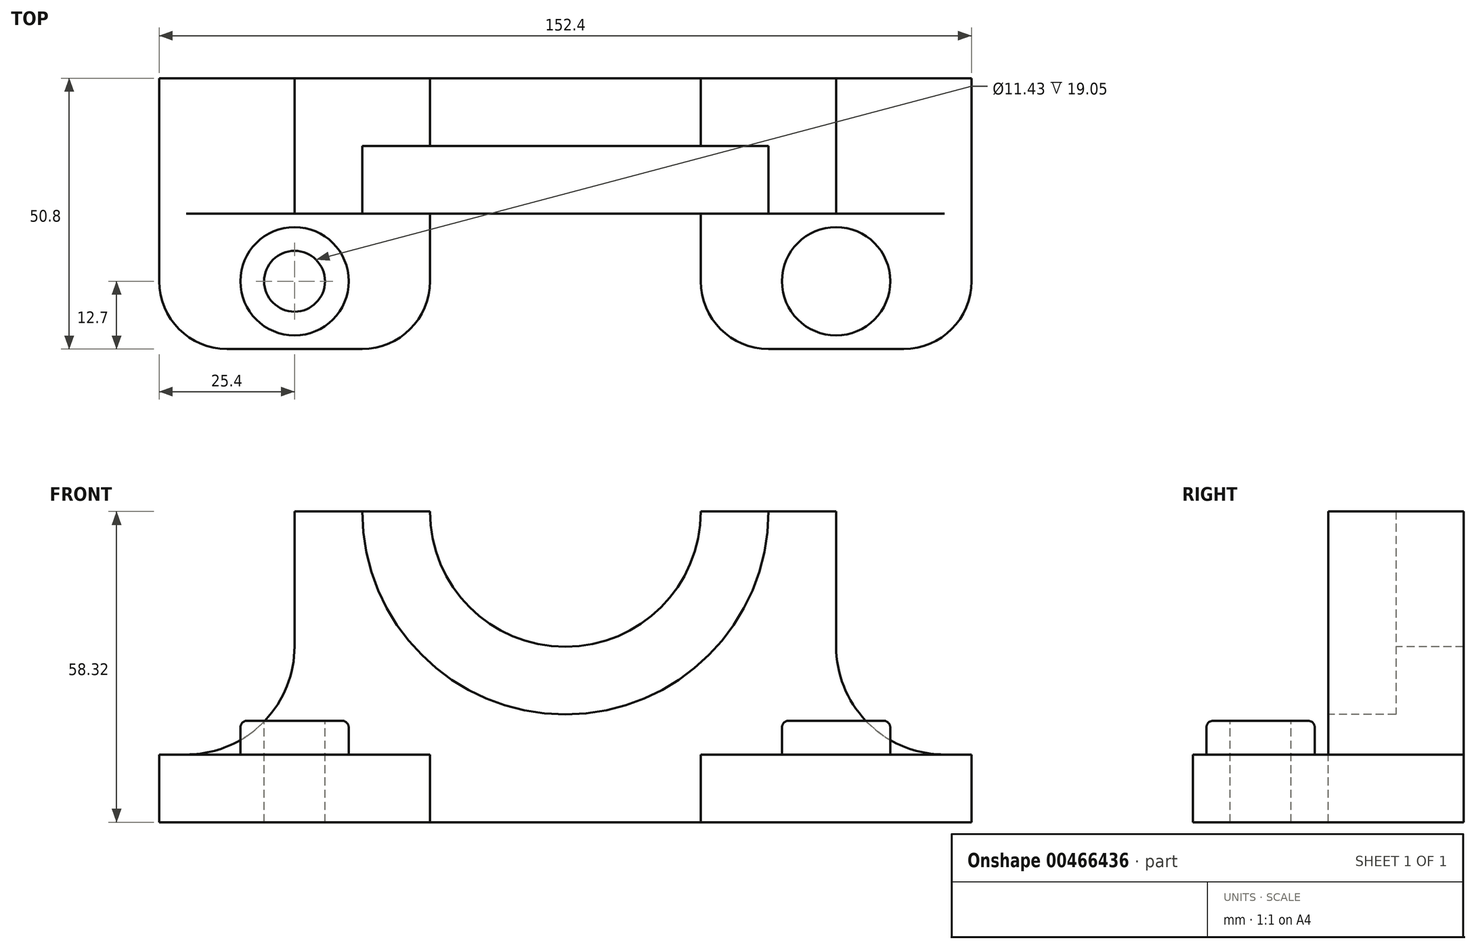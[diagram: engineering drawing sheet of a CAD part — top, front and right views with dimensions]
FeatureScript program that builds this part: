
annotation { "Feature Type Name" : "Feature", "Feature Type Description" : "" }
export const myFeature = defineFeature(function(context is Context, id is Id, definition is map)
    precondition{}
    {
        {
            var Q0;
            Q0=qCreatedBy(makeId("Front.planeOp"),FACE);
            var sketch = newSketch(context, id + "F0", { "sketchPlane" : qUnion([Q0])});
            skLineSegment(sketch, "E0.bottom", {"start": v(-50.8, 0) * mm, "end": v(50.8, 0) * mm});
            skLineSegment(sketch, "E0.top", {"start": v(-50.8, 58.32) * mm, "end": v(50.8, 58.32) * mm});
            skLineSegment(sketch, "E0.left", {"start": v(-50.8, 0) * mm, "end": v(-50.8, 58.32) * mm});
            skLineSegment(sketch, "E0.right", {"start": v(50.8, 0) * mm, "end": v(50.8, 58.32) * mm});
            skSolve(sketch);
        }
        {
            var Q0;
            Q0=qCreatedBy(makeId("Front.planeOp"),FACE);
            var sketch = newSketch(context, id + "F1", { "sketchPlane" : qUnion([Q0])});
            skLineSegment(sketch, "E1.bottom", {"start": v(-76.2, 12.7) * mm, "end": v(-25.4, 12.7) * mm});
            skLineSegment(sketch, "E1.top", {"start": v(-76.2, 0) * mm, "end": v(-25.4, 0) * mm});
            skLineSegment(sketch, "E1.left", {"start": v(-76.2, 12.7) * mm, "end": v(-76.2, 0) * mm});
            skLineSegment(sketch, "E1.right", {"start": v(-25.4, 12.7) * mm, "end": v(-25.4, 0) * mm});
            skLineSegment(sketch, "E2.MirrorCS", {"start": v(76.2, 12.7) * mm, "end": v(25.4, 12.7) * mm});
            skLineSegment(sketch, "E3.MirrorCS", {"start": v(76.2, 12.7) * mm, "end": v(76.2, 0) * mm});
            skLineSegment(sketch, "E4.MirrorCS", {"start": v(76.2, 0) * mm, "end": v(25.4, 0) * mm});
            skLineSegment(sketch, "E5.MirrorCS", {"start": v(25.4, 12.7) * mm, "end": v(25.4, 0) * mm});
            skSolve(sketch);
        }
        {
            var Q0;
            Q0=makeQuery(id+"F0.imprint","IMPRINT",FACE,{"disambiguationData":[TD([[makeQuery(id+"F0.imprint","IMPRINT",EDGE,{"derivedFrom":sQuery(id+"F0.wireOp",EDGE,"E0.bottom")}),1.0]])]});
            extrude(context, id + "F2", {"entities" : qUnion([Q0]), "depth" : 25.4 * mm});
        }
        {
            var Q0;
            Q0=makeQuery(id+"F1.imprint","IMPRINT",FACE,{"disambiguationData":[TD([[makeQuery(id+"F1.imprint","IMPRINT",EDGE,{"derivedFrom":sQuery(id+"F1.wireOp",EDGE,"E1.bottom")}),-1.0]])]});
            var Q1;
            Q1=makeQuery(id+"F1.imprint","IMPRINT",FACE,{"disambiguationData":[TD([[makeQuery(id+"F1.imprint","IMPRINT",EDGE,{"derivedFrom":sQuery(id+"F1.wireOp",EDGE,"E2.MirrorCS")}),1.0]])]});
            extrude(context, id + "F3", {"entities" : qUnion([Q0, Q1]), "operationType" : NewBodyOperationType.ADD, "depth" : 50.8 * mm});
        }
        {
            var Q0;
            Q0=makeQuery(id+"F3.opExtrude","SWEPT_FACE",FACE,{"disambiguationData":[OSD([sQuery(id+"F1.wireOp",EDGE,"E1.bottom")])]});
            var sketch = newSketch(context, id + "F4", { "sketchPlane" : qUnion([Q0])});
            skLineSegment(sketch, "E6", {"start": v(-50.8, -25.4) * mm, "end": v(-50.8, -50.8) * mm, "construction": true});
            skCircle(sketch, "E7", {"center": v(-50.8, -38.1) * mm, "radius": 10.16 * mm});
            skSolve(sketch);
        }
        {
            var Q0;
            Q0=makeQuery(id+"F3.opExtrude","CAP_EDGE",EDGE,{"disambiguationData":[OSD([sQuery(id+"F1.wireOp",EDGE,"E1.left")])],"isStart":false});
            var Q1;
            Q1=makeQuery(id+"F3.opExtrude","CAP_EDGE",EDGE,{"disambiguationData":[OSD([sQuery(id+"F1.wireOp",EDGE,"E1.right")])],"isStart":false});
            var Q2;
            Q2=makeQuery(id+"F3.opExtrude","CAP_EDGE",EDGE,{"disambiguationData":[OSD([sQuery(id+"F1.wireOp",EDGE,"E5.MirrorCS")])],"isStart":false});
            var Q3;
            Q3=makeQuery(id+"F3.opExtrude","CAP_EDGE",EDGE,{"disambiguationData":[OSD([sQuery(id+"F1.wireOp",EDGE,"E3.MirrorCS")])],"isStart":false});
            fillet(context, id + "F5", {"entities" : qUnion([Q0, Q1, Q2, Q3]), "radius" : 12.7 * mm, "tangentPropagation" : true, "allowEdgeOverflow" : false});
        }
        {
            var Q0;
            Q0=makeQuery(id+"F4.imprint","IMPRINT",FACE,{"disambiguationData":[TD([[makeQuery(id+"F4.imprint","IMPRINT",EDGE,{"derivedFrom":sQuery(id+"F4.wireOp",EDGE,"E7")}),1.0]])]});
            extrude(context, id + "F6", {"entities" : qUnion([Q0]), "operationType" : NewBodyOperationType.ADD, "depth" : 6.35 * mm});
        }
        {
            var Q0;
            Q0=makeQuery(id+"F2.opExtrude","SWEPT_BODY",BODY,{"disambiguationData":[OSD([sQuery(id+"F0.wireOp",EDGE,"E0.bottom"),sQuery(id+"F0.wireOp",EDGE,"E0.top"),sQuery(id+"F0.wireOp",EDGE,"E0.left"),sQuery(id+"F0.wireOp",EDGE,"E0.right")])]});
            var Q1;
            Q1=qCreatedBy(makeId("Right.planeOp"),FACE);
            mirror(context, id + "F7", {"operationType" : NewBodyOperationType.ADD, "entities" : qUnion([Q0]), "mirrorPlane" : qUnion([Q1])});
        }
        {
            var Q0;
            Q0=makeQuery(id+"F6.opExtrude","CAP_EDGE",EDGE,{"disambiguationData":[OSD([sQuery(id+"F4.wireOp",EDGE,"E7")])],"isStart":false});
            var Q1;
            Q1=makeQuery(id+"F7.opPattern","COPY",EDGE,{"derivedFrom":makeQuery(id+"F6.opExtrude","CAP_EDGE",EDGE,{"disambiguationData":[OSD([sQuery(id+"F4.wireOp",EDGE,"E7")])],"isStart":false}),"instanceName":"1"});
            fillet(context, id + "F8", {"entities" : qUnion([Q0, Q1]), "radius" : 1.27 * mm, "tangentPropagation" : true, "allowEdgeOverflow" : false});
        }
        {
            var Q0;
            Q0=makeQuery(id+"F2.opExtrude","CAP_FACE",FACE,{"disambiguationData":[OSD([sQuery(id+"F0.wireOp",EDGE,"E0.bottom"),sQuery(id+"F0.wireOp",EDGE,"E0.top"),sQuery(id+"F0.wireOp",EDGE,"E0.left"),sQuery(id+"F0.wireOp",EDGE,"E0.right")])],"isStart":false});
            var sketch = newSketch(context, id + "F9", { "sketchPlane" : qUnion([Q0])});
            skCircle(sketch, "E8", {"center": v(0, 58.32) * mm, "radius": 38.1 * mm});
            skSolve(sketch);
        }
        {
            var Q0;
            {var subQ0=sQuery(id+"F9.wireOp",EDGE,"E8");var subQ1=makeQuery(id+"F2.opExtrude","CAP_EDGE",EDGE,{"disambiguationData":[OSD([sQuery(id+"F0.wireOp",EDGE,"E0.top")])],"isStart":false});var subQ2=makeQuery(id+"F9.imprint","INTERSECT",VERTEX,{"disambiguationData":[OD(0.0)],"derivedFrom":[subQ1,subQ0]});Q0=makeQuery(id+"F9.imprint","IMPRINT",FACE,{"disambiguationData":[TD([[makeQuery(id+"F9.imprint","IMPRINT",EDGE,{"disambiguationData":[TD([[subQ2,-1.0]])],"derivedFrom":subQ0}),1.0]])]});}
            extrude(context, id + "F10", {"entities" : qUnion([Q0]), "operationType" : NewBodyOperationType.REMOVE, "oppositeDirection" : true, "depth" : 12.7 * mm});
        }
        {
            var Q0;
            Q0=makeQuery(id+"F10.boolean.opBoolean","COPY",FACE,{"derivedFrom":makeQuery(id+"F10.opExtrude","CAP_FACE",FACE,{"disambiguationData":[OSD([sQuery(id+"F0.wireOp",EDGE,"E0.top"),sQuery(id+"F9.wireOp",EDGE,"E8")])],"isStart":false})});
            var sketch = newSketch(context, id + "F11", { "sketchPlane" : qUnion([Q0])});
            skCircle(sketch, "E9", {"center": v(0, 58.32) * mm, "radius": 25.4 * mm});
            skSolve(sketch);
        }
        {
            var Q0;
            {var subQ0=sQuery(id+"F11.wireOp",EDGE,"E9");var subQ1=makeQuery(id+"F10.boolean.opBoolean","COPY",EDGE,{"derivedFrom":makeQuery(id+"F10.opExtrude","CAP_EDGE",EDGE,{"disambiguationData":[OSD([sQuery(id+"F0.wireOp",EDGE,"E0.top")])],"isStart":false})});var subQ2=makeQuery(id+"F11.imprint","INTERSECT",VERTEX,{"disambiguationData":[OD(0.0)],"derivedFrom":[subQ1,subQ0]});Q0=makeQuery(id+"F11.imprint","IMPRINT",FACE,{"disambiguationData":[TD([[makeQuery(id+"F11.imprint","IMPRINT",EDGE,{"disambiguationData":[TD([[subQ2,-1.0]])],"derivedFrom":subQ0}),1.0]])]});}
            extrude(context, id + "F12", {"entities" : qUnion([Q0]), "operationType" : NewBodyOperationType.REMOVE, "endBound" : BoundingType.THROUGH_ALL, "oppositeDirection" : true, "depth" : 25.4 * mm});
        }
        {
            var Q0;
            Q0=makeQuery(id+"F3.boolean.opBoolean","INTERSECT",EDGE,{"derivedFrom":[makeQuery(id+"F2.opExtrude","SWEPT_FACE",FACE,{"disambiguationData":[OSD([sQuery(id+"F0.wireOp",EDGE,"E0.right")])]}),makeQuery(id+"F3.opExtrude","SWEPT_FACE",FACE,{"disambiguationData":[OSD([sQuery(id+"F1.wireOp",EDGE,"E2.MirrorCS")])]})]});
            var Q1;
            Q1=makeQuery(id+"F3.boolean.opBoolean","INTERSECT",EDGE,{"derivedFrom":[makeQuery(id+"F2.opExtrude","SWEPT_FACE",FACE,{"disambiguationData":[OSD([sQuery(id+"F0.wireOp",EDGE,"E0.left")])]}),makeQuery(id+"F3.opExtrude","SWEPT_FACE",FACE,{"disambiguationData":[OSD([sQuery(id+"F1.wireOp",EDGE,"E1.bottom")])]})]});
            fillet(context, id + "F13", {"entities" : qUnion([Q0, Q1]), "radius" : 20.32 * mm, "tangentPropagation" : true, "allowEdgeOverflow" : false});
        }
        {
            var Q0;
            Q0=makeQuery(id+"F6.opExtrude","CAP_FACE",FACE,{"disambiguationData":[OSD([sQuery(id+"F4.wireOp",EDGE,"E7")])],"isStart":false});
            var sketch = newSketch(context, id + "F14", { "sketchPlane" : qUnion([Q0])});
            skCircle(sketch, "E10", {"center": v(-50.8, -38.1) * mm, "radius": 5.72 * mm});
            skCircle(sketch, "E11.MirrorC", {"center": v(50.8, -38.1) * mm, "radius": 5.72 * mm});
            skSolve(sketch);
        }
        {
            var Q0;
            Q0=makeQuery(id+"F14.imprint","IMPRINT",FACE,{"disambiguationData":[TD([[makeQuery(id+"F14.imprint","IMPRINT",EDGE,{"derivedFrom":sQuery(id+"F14.wireOp",EDGE,"E10")}),1.0]])]});
            var Q1;
            Q1=makeQuery(id+"F14.imprint","IMPRINT",FACE,{"disambiguationData":[TD([[makeQuery(id+"F14.imprint","IMPRINT",EDGE,{"derivedFrom":sQuery(id+"F14.wireOp",EDGE,"E11.MirrorC")}),-1.0]])]});
            extrude(context, id + "F15", {"entities" : qUnion([Q0, Q1]), "operationType" : NewBodyOperationType.REMOVE, "endBound" : BoundingType.THROUGH_ALL, "oppositeDirection" : true, "depth" : 25.4 * mm});
        }
    });
